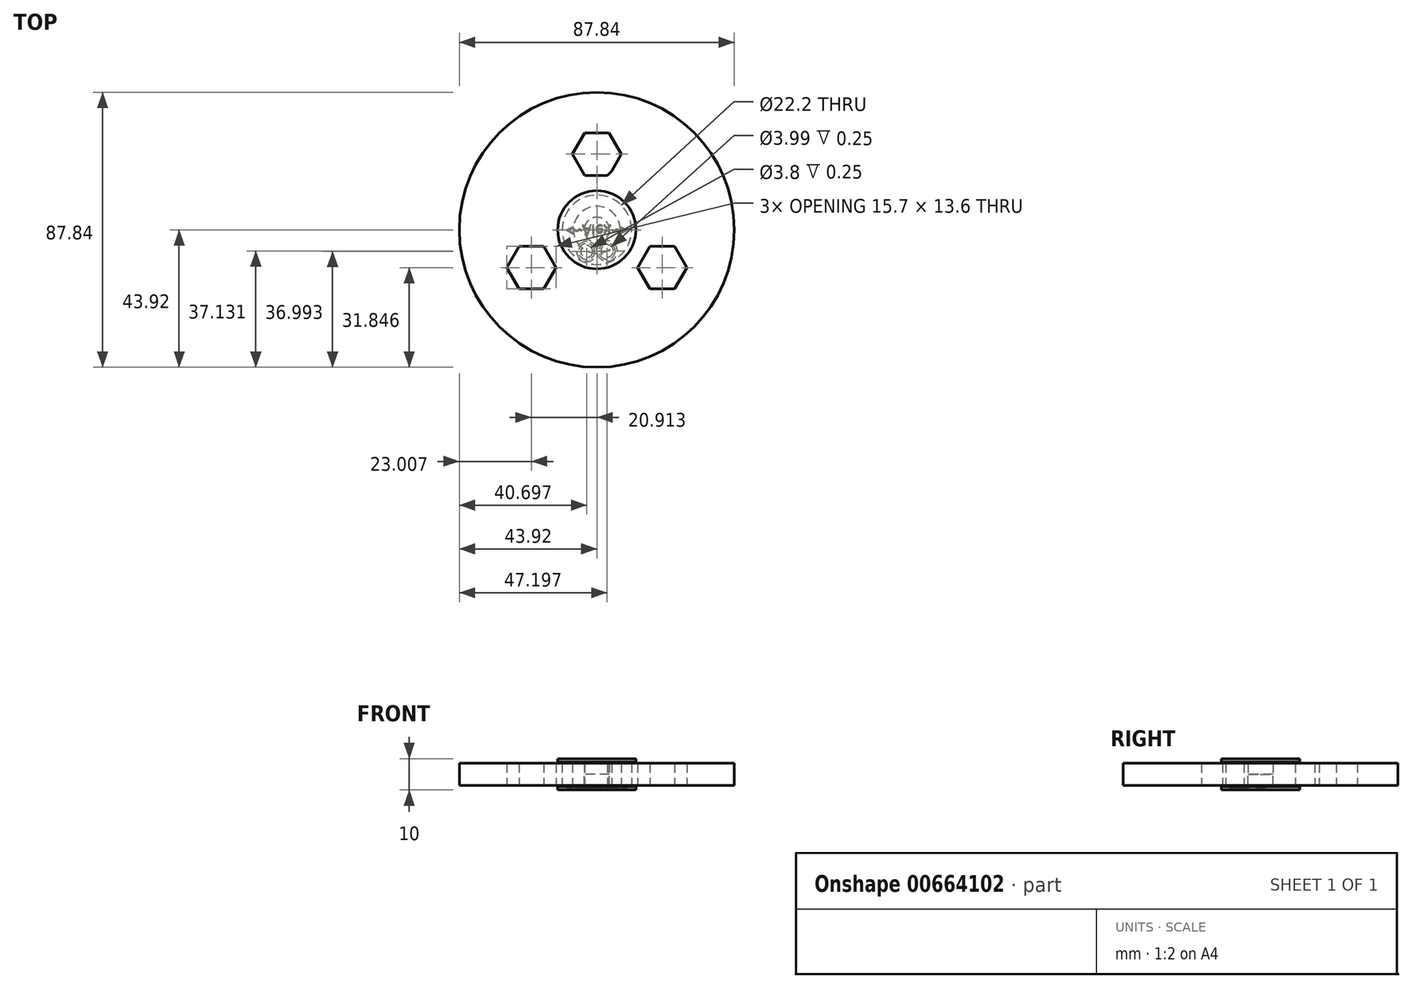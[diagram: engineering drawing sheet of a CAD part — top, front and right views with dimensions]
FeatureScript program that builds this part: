
annotation { "Feature Type Name" : "Feature", "Feature Type Description" : "" }
export const myFeature = defineFeature(function(context is Context, id is Id, definition is map)
    precondition{}
    {
        {
            var Q0;
            Q0=qCreatedBy(makeId("Top.planeOp"),FACE);
            var sketch = newSketch(context, id + "F0", { "sketchPlane" : qUnion([Q0])});
            skCircle(sketch, "E0", {"center": v(0, 0) * mm, "radius": 11.1 * mm});
            skCircle(sketch, "E1", {"center": v(0, 0) * mm, "radius": 4 * mm});
            skCircle(sketch, "E2.cCircle", {"center": v(0, 24.15) * mm, "radius": 6.8 * mm, "construction": true});
            skLineSegment(sketch, "E2.0", {"start": v(3.93, 17.35) * mm, "end": v(-3.93, 17.35) * mm});
            skLineSegment(sketch, "E2.1", {"start": v(-3.93, 17.35) * mm, "end": v(-7.85, 24.15) * mm});
            skLineSegment(sketch, "E2.2", {"start": v(-7.85, 24.15) * mm, "end": v(-3.93, 30.95) * mm});
            skLineSegment(sketch, "E2.3", {"start": v(-3.93, 30.95) * mm, "end": v(3.93, 30.95) * mm});
            skLineSegment(sketch, "E2.4", {"start": v(3.93, 30.95) * mm, "end": v(7.85, 24.15) * mm});
            skLineSegment(sketch, "E2.5", {"start": v(7.85, 24.15) * mm, "end": v(3.93, 17.35) * mm});
            skPoint(sketch, "E2.0.midPoint", {"position": v(0, 17.35) * mm});
            skLineSegment(sketch, "E3", {"start": v(0, 0) * mm, "end": v(0, 35) * mm, "construction": true});
            skArc(sketch, "E4", {"start": v(-11.18, 8.6) * mm, "mid": v(-12.21, 7.05) * mm, "end": v(-13.03, 5.38) * mm});
            skArc(sketch, "E5", {"start": v(-11.18, 8.6) * mm, "mid": v(-9, 13.96) * mm, "end": v(-9.89, 19.68) * mm});
            skArc(sketch, "E6", {"start": v(9.89, 19.68) * mm, "mid": v(9, 13.96) * mm, "end": v(11.18, 8.6) * mm});
            skArc(sketch, "E7.trimOffspring", {"start": v(9.89, 19.68) * mm, "mid": v(0, 35) * mm, "end": v(-9.89, 19.68) * mm});
            skArc(sketch, "E8.1.0", {"start": v(-1.86, -13.98) * mm, "mid": v(-7.59, -14.77) * mm, "end": v(-12.1, -18.4) * mm});
            skArc(sketch, "E8.1.1", {"start": v(-21.99, -1.28) * mm, "mid": v(-30.31, -17.5) * mm, "end": v(-12.1, -18.4) * mm});
            skLineSegment(sketch, "E8.1.2", {"start": v(-13.06, -12.07) * mm, "end": v(-16.99, -18.87) * mm});
            skLineSegment(sketch, "E8.1.3", {"start": v(-16.99, -18.87) * mm, "end": v(-24.84, -18.87) * mm});
            skLineSegment(sketch, "E8.1.4", {"start": v(-24.84, -18.87) * mm, "end": v(-28.76, -12.07) * mm});
            skLineSegment(sketch, "E8.1.5", {"start": v(-28.76, -12.07) * mm, "end": v(-24.84, -5.27) * mm});
            skLineSegment(sketch, "E8.1.6", {"start": v(-24.84, -5.27) * mm, "end": v(-16.99, -5.27) * mm});
            skLineSegment(sketch, "E8.1.7", {"start": v(-16.99, -5.27) * mm, "end": v(-13.06, -12.07) * mm});
            skArc(sketch, "E8.1.8", {"start": v(-21.99, -1.28) * mm, "mid": v(-16.59, 0.81) * mm, "end": v(-13.03, 5.38) * mm});
            skArc(sketch, "E8.2.0", {"start": v(13.03, 5.38) * mm, "mid": v(16.59, 0.81) * mm, "end": v(21.99, -1.28) * mm});
            skArc(sketch, "E8.2.1", {"start": v(12.1, -18.4) * mm, "mid": v(30.31, -17.5) * mm, "end": v(21.99, -1.28) * mm});
            skLineSegment(sketch, "E8.2.2", {"start": v(16.99, -5.27) * mm, "end": v(24.84, -5.27) * mm});
            skLineSegment(sketch, "E8.2.3", {"start": v(24.84, -5.27) * mm, "end": v(28.76, -12.07) * mm});
            skLineSegment(sketch, "E8.2.4", {"start": v(28.76, -12.07) * mm, "end": v(24.84, -18.87) * mm});
            skLineSegment(sketch, "E8.2.5", {"start": v(24.84, -18.87) * mm, "end": v(16.99, -18.87) * mm});
            skLineSegment(sketch, "E8.2.6", {"start": v(16.99, -18.87) * mm, "end": v(13.06, -12.07) * mm});
            skLineSegment(sketch, "E8.2.7", {"start": v(13.06, -12.07) * mm, "end": v(16.99, -5.27) * mm});
            skArc(sketch, "E8.2.8", {"start": v(12.1, -18.4) * mm, "mid": v(7.59, -14.77) * mm, "end": v(1.86, -13.98) * mm});
            skArc(sketch, "E9.trimOffspring", {"start": v(-1.86, -13.98) * mm, "mid": v(0, -14.1) * mm, "end": v(1.86, -13.98) * mm});
            skArc(sketch, "E10.trimOffspring", {"start": v(13.03, 5.38) * mm, "mid": v(12.21, 7.05) * mm, "end": v(11.18, 8.6) * mm});
            skArc(sketch, "E11", {"start": v(-13.03, 5.38) * mm, "mid": v(-14.09, 0.64) * mm, "end": v(-13.47, -4.18) * mm});
            skArc(sketch, "E12", {"start": v(11.18, 8.6) * mm, "mid": v(7.6, 11.88) * mm, "end": v(3.11, 13.75) * mm});
            skArc(sketch, "E13", {"start": v(1.86, -13.98) * mm, "mid": v(6.49, -12.52) * mm, "end": v(10.35, -9.57) * mm});
            skArc(sketch, "E14", {"start": v(-12.1, -18.4) * mm, "mid": v(-10.27, -14.18) * mm, "end": v(-10.35, -9.57) * mm});
            skArc(sketch, "E15", {"start": v(-9.89, 19.68) * mm, "mid": v(-7.14, 15.98) * mm, "end": v(-3.11, 13.75) * mm});
            skArc(sketch, "E16", {"start": v(21.99, -1.28) * mm, "mid": v(17.41, -1.8) * mm, "end": v(13.47, -4.18) * mm});
            skLineSegment(sketch, "E17", {"start": v(0, 24.15) * mm, "end": v(5.43, 33.55) * mm, "construction": true});
            skArc(sketch, "E18.trimOffspring", {"start": v(-13.47, -4.18) * mm, "mid": v(-17.41, -1.8) * mm, "end": v(-21.99, -1.28) * mm});
            skArc(sketch, "E19.trimOffspring", {"start": v(10.35, -9.57) * mm, "mid": v(10.27, -14.18) * mm, "end": v(12.1, -18.4) * mm});
            skArc(sketch, "E20.trimOffspring", {"start": v(3.11, 13.75) * mm, "mid": v(7.14, 15.98) * mm, "end": v(9.89, 19.68) * mm});
            skCircle(sketch, "E21", {"center": v(0, 0) * mm, "radius": 7.5 * mm});
            skCircle(sketch, "E22", {"center": v(0, 0) * mm, "radius": 12.5 * mm});
            skArc(sketch, "E23.trimOffspring", {"start": v(-3.11, 13.75) * mm, "mid": v(-7.6, 11.88) * mm, "end": v(-11.18, 8.6) * mm});
            skArc(sketch, "E24.trimOffspring", {"start": v(-10.35, -9.57) * mm, "mid": v(-6.49, -12.52) * mm, "end": v(-1.86, -13.98) * mm});
            skArc(sketch, "E25.trimOffspring", {"start": v(13.47, -4.18) * mm, "mid": v(14.09, 0.64) * mm, "end": v(13.03, 5.38) * mm});
            skSolve(sketch);
        }
        {
            var Q0;
            {var subQ1=sQuery(id+"F0.wireOp",EDGE,"E8.1.1");Q0=makeQuery(id+"F0.imprint","IMPRINT",FACE,{"disambiguationData":[TD([[makeQuery(id+"F0.imprint","IMPRINT",EDGE,{"derivedFrom":subQ1}),1.0]])]});}
            var Q1;
            {var subQ0=sQuery(id+"F0.wireOp",EDGE,"E8.1.8");Q1=makeQuery(id+"F0.imprint","IMPRINT",FACE,{"disambiguationData":[TD([[makeQuery(id+"F0.imprint","IMPRINT",EDGE,{"derivedFrom":subQ0}),-1.0]])]});}
            var Q2;
            Q2=makeQuery(id+"F0.imprint","IMPRINT",FACE,{"disambiguationData":[TD([[makeQuery(id+"F0.imprint","IMPRINT",EDGE,{"derivedFrom":sQuery(id+"F0.wireOp",EDGE,"E0")}),-1.0]])]});
            var Q3;
            {var subQ0=sQuery(id+"F0.wireOp",EDGE,"E5");Q3=makeQuery(id+"F0.imprint","IMPRINT",FACE,{"disambiguationData":[TD([[makeQuery(id+"F0.imprint","IMPRINT",EDGE,{"derivedFrom":subQ0}),-1.0]])]});}
            var Q4;
            Q4=makeQuery(id+"F0.imprint","IMPRINT",FACE,{"disambiguationData":[TD([[makeQuery(id+"F0.imprint","IMPRINT",EDGE,{"derivedFrom":sQuery(id+"F0.wireOp",EDGE,"E2.0")}),1.0]])]});
            var Q5;
            {var subQ0=sQuery(id+"F0.wireOp",EDGE,"E8.1.0");Q5=makeQuery(id+"F0.imprint","IMPRINT",FACE,{"disambiguationData":[TD([[makeQuery(id+"F0.imprint","IMPRINT",EDGE,{"derivedFrom":subQ0}),-1.0]])]});}
            var Q6;
            {var subQ0=sQuery(id+"F0.wireOp",EDGE,"E8.2.0");Q6=makeQuery(id+"F0.imprint","IMPRINT",FACE,{"disambiguationData":[TD([[makeQuery(id+"F0.imprint","IMPRINT",EDGE,{"derivedFrom":subQ0}),-1.0]])]});}
            var Q7;
            {var subQ0=sQuery(id+"F0.wireOp",EDGE,"E8.2.8");Q7=makeQuery(id+"F0.imprint","IMPRINT",FACE,{"disambiguationData":[TD([[makeQuery(id+"F0.imprint","IMPRINT",EDGE,{"derivedFrom":subQ0}),-1.0]])]});}
            var Q8;
            {var subQ0=sQuery(id+"F0.wireOp",EDGE,"E8.2.1");Q8=makeQuery(id+"F0.imprint","IMPRINT",FACE,{"disambiguationData":[TD([[makeQuery(id+"F0.imprint","IMPRINT",EDGE,{"derivedFrom":subQ0}),1.0]])]});}
            var Q9;
            {var subQ0=sQuery(id+"F0.wireOp",EDGE,"E6");Q9=makeQuery(id+"F0.imprint","IMPRINT",FACE,{"disambiguationData":[TD([[makeQuery(id+"F0.imprint","IMPRINT",EDGE,{"derivedFrom":subQ0}),-1.0]])]});}
            var Q10;
            {var subQ4=sQuery(id+"F0.wireOp",EDGE,"E4");Q10=makeQuery(id+"F0.imprint","IMPRINT",FACE,{"disambiguationData":[TD([[makeQuery(id+"F0.imprint","IMPRINT",EDGE,{"derivedFrom":subQ4}),1.0]])]});}
            extrude(context, id + "F1", {"entities" : qUnion([Q0, Q1, Q2, Q3, Q4, Q5, Q6, Q7, Q8, Q9, Q10]), "endBound" : BoundingType.SYMMETRIC, "depth" : 3 * mm, "offsetDistance" : 25 * mm});
        }
        {
            var Q0;
            Q0=makeQuery(id+"F0.imprint","IMPRINT",FACE,{"disambiguationData":[TD([[makeQuery(id+"F0.imprint","IMPRINT",EDGE,{"derivedFrom":sQuery(id+"F0.wireOp",EDGE,"E0")}),-1.0]])]});
            var Q1;
            Q1=makeQuery(id+"F0.imprint","IMPRINT",FACE,{"disambiguationData":[TD([[makeQuery(id+"F0.imprint","IMPRINT",EDGE,{"derivedFrom":sQuery(id+"F0.wireOp",EDGE,"E2.0")}),1.0]])]});
            extrude(context, id + "F2", {"entities" : qUnion([Q0, Q1]), "operationType" : NewBodyOperationType.ADD, "endBound" : BoundingType.SYMMETRIC, "oppositeDirection" : true, "depth" : 7 * mm, "offsetDistance" : 25 * mm});
        }
        {
            var Q0;
            Q0=makeQuery(id+"F0.imprint","IMPRINT",FACE,{"disambiguationData":[TD([[makeQuery(id+"F0.imprint","IMPRINT",EDGE,{"derivedFrom":sQuery(id+"F0.wireOp",EDGE,"E1")}),1.0]])]});
            extrude(context, id + "F3", {"entities" : qUnion([Q0]), "depth" : 3.5 * mm, "offsetDistance" : 25 * mm});
        }
        {
            var Q0;
            Q0=makeQuery(id+"F0.imprint","IMPRINT",FACE,{"disambiguationData":[TD([[makeQuery(id+"F0.imprint","IMPRINT",EDGE,{"derivedFrom":sQuery(id+"F0.wireOp",EDGE,"E1")}),1.0]])]});
            var Q1;
            Q1=makeQuery(id+"F0.imprint","IMPRINT",FACE,{"disambiguationData":[TD([[makeQuery(id+"F0.imprint","IMPRINT",EDGE,{"derivedFrom":sQuery(id+"F0.wireOp",EDGE,"E1")}),-1.0]])]});
            var Q2;
            Q2=makeQuery(id+"F3.opExtrude","CAP_FACE",FACE,{"disambiguationData":[OSD([sQuery(id+"F0.wireOp",EDGE,"E1")])],"isStart":false});
            extrude(context, id + "F4", {"entities" : qUnion([Q0, Q1]), "operationType" : NewBodyOperationType.ADD, "depth" : 4 * mm, "offsetDistance" : 25 * mm, "hasSecondDirection" : true, "secondDirectionBound" : SecondDirectionBoundingType.UP_TO_SURFACE, "secondDirectionOppositeDirection" : false, "secondDirectionDepth" : 25 * mm, "secondDirectionBoundEntityFace" : qUnion([Q2])});
        }
        {
            var Q0;
            Q0=makeQuery(id+"F0.imprint","IMPRINT",FACE,{"disambiguationData":[TD([[makeQuery(id+"F0.imprint","IMPRINT",EDGE,{"derivedFrom":sQuery(id+"F0.wireOp",EDGE,"E0")}),-1.0]])]});
            var Q1;
            Q1=makeQuery(id+"F0.imprint","IMPRINT",FACE,{"disambiguationData":[TD([[makeQuery(id+"F0.imprint","IMPRINT",EDGE,{"derivedFrom":sQuery(id+"F0.wireOp",EDGE,"E0")}),1.0]])]});
            var Q2;
            Q2=makeQuery(id+"F0.imprint","IMPRINT",FACE,{"disambiguationData":[TD([[makeQuery(id+"F0.imprint","IMPRINT",EDGE,{"derivedFrom":sQuery(id+"F0.wireOp",EDGE,"E1")}),-1.0]])]});
            var Q3;
            Q3=makeQuery(id+"F0.imprint","IMPRINT",FACE,{"disambiguationData":[TD([[makeQuery(id+"F0.imprint","IMPRINT",EDGE,{"derivedFrom":sQuery(id+"F0.wireOp",EDGE,"E1")}),1.0]])]});
            var Q4;
            Q4=makeQuery(id+"F4.opExtrude","CAP_FACE",FACE,{"disambiguationData":[OSD([sQuery(id+"F0.wireOp",EDGE,"E21")])],"isStart":false});
            extrude(context, id + "F5", {"entities" : qUnion([Q0, Q1, Q2, Q3]), "operationType" : NewBodyOperationType.ADD, "depth" : 5 * mm, "offsetDistance" : 25 * mm, "hasSecondDirection" : true, "secondDirectionBound" : SecondDirectionBoundingType.UP_TO_SURFACE, "secondDirectionOppositeDirection" : false, "secondDirectionDepth" : 25 * mm, "secondDirectionBoundEntityFace" : qUnion([Q4])});
        }
        {
            var Q0;
            Q0=makeQuery(id+"F3.opExtrude","SWEPT_BODY",BODY,{"disambiguationData":[OSD([sQuery(id+"F0.wireOp",EDGE,"E1")])]});
            var Q1;
            Q1=makeQuery(id+"F3.opExtrude","CAP_FACE",FACE,{"disambiguationData":[OSD([sQuery(id+"F0.wireOp",EDGE,"E1")])],"isStart":true});
            mirror(context, id + "F6", {"entities" : qUnion([Q0]), "mirrorPlane" : qUnion([Q1])});
        }
        {
            var Q0;
            Q0=makeQuery(id+"F6.opPattern","COPY",FACE,{"derivedFrom":makeQuery(id+"F5.opExtrude","CAP_FACE",FACE,{"disambiguationData":[OSD([sQuery(id+"F0.wireOp",EDGE,"E22")])],"isStart":false}),"instanceName":"1"});
            var sketch = newSketch(context, id + "F7", { "sketchPlane" : qUnion([Q0])});
            skText(sketch, "E26", { "text": "<~Alex~>", "fontName": "OpenSans-Regular.ttf"});
            skPoint(sketch, "E27", {"position": v(0, -12.5) * mm});
            skPoint(sketch, "E28", {"position": v(-12.5, 0) * mm});
            const initialGuessF7  = {"E26": [-0.01, -0.0015, 1, 0, 0.00337]};
            skSetInitialGuess(sketch, initialGuessF7);
            skSolve(sketch);
        }
        {
            var Q0;
            Q0=makeQuery(id+"F7.imprint","IMPRINT",FACE,{"disambiguationData":[TD([[makeQuery(id+"F7.imprint","IMPRINT",EDGE,{"derivedFrom":sQuery(id+"F7.wireOp",EDGE,"E26.sketch_text.stroke-0")}),1.0]])]});
            var sketch = newSketch(context, id + "F8", { "sketchPlane" : qUnion([Q0])});
            skArc(sketch, "E29", {"start": v(0.04, 6.25) * mm, "mid": v(6.55, 6.67) * mm, "end": v(0.1, 7.57) * mm});
            skPoint(sketch, "E30.center.orphan", {"position": v(0, 6.93) * mm});
            skCircle(sketch, "E31", {"center": v(-3.22, 6.93) * mm, "radius": 2.57 * mm});
            skCircle(sketch, "E32", {"center": v(3.28, 6.79) * mm, "radius": 2.62 * mm});
            skLineSegment(sketch, "E33.trimOffspring", {"start": v(-0.07, 7.62) * mm, "end": v(-0.07, 7.62) * mm});
            skPoint(sketch, "E34.1.internal.orphan", {"position": v(0.1, 7.15) * mm});
            skArc(sketch, "E35", {"start": v(-0.07, 7.62) * mm, "mid": v(-6.45, 6.97) * mm, "end": v(-0.1, 6.14) * mm});
            skFitSpline(sketch, "E36", {"points": [v(-0.07, 7.62) * mm, v(0, 7.34) * mm, v(0.1, 7.57) * mm, v(0.3, 7.07) * mm, v(0.3, 6.56) * mm, v(0.3, 6.34) * mm], "startDerivative": vector(0.4, -2.54) * mm, "endDerivative": vector(0.05, -1.27) * mm});
            skFitSpline(sketch, "E37", {"points": [v(-0.1, 6.14) * mm, v(0, 6.43) * mm, v(0.04, 6.25) * mm], "startDerivative": vector(0.2, 0.78) * mm, "endDerivative": vector(0.08, -0.63) * mm});
            skPoint(sketch, "E38.3.internal.orphan", {"position": v(0.04, 6.93) * mm});
            skPoint(sketch, "E38.4.internal.orphan", {"position": v(-0.1, 7.15) * mm});
            skPoint(sketch, "E38.endDerivative.orphan", {"position": v(0.3, 6.89) * mm});
            skCircle(sketch, "E39", {"center": v(-3.22, 6.93) * mm, "radius": 1.9 * mm});
            skCircle(sketch, "E40", {"center": v(3.28, 6.79) * mm, "radius": 2 * mm});
            skLineSegment(sketch, "E41", {"start": v(-12.67, 0) * mm, "end": v(21.78, 0) * mm});
            skLineSegment(sketch, "E42", {"start": v(21.78, 0) * mm, "end": v(16.86, 11.11) * mm});
            skArc(sketch, "E43.MirrorCS", {"start": v(0.04, -6.25) * mm, "mid": v(6.55, -6.67) * mm, "end": v(0.1, -7.57) * mm});
            skArc(sketch, "E44.MirrorCS", {"start": v(-0.07, -7.62) * mm, "mid": v(-6.45, -6.97) * mm, "end": v(-0.1, -6.14) * mm});
            skCircle(sketch, "E45.MirrorC", {"center": v(-3.22, -6.93) * mm, "radius": 2.57 * mm});
            skCircle(sketch, "E46.MirrorC", {"center": v(-3.22, -6.93) * mm, "radius": 1.9 * mm});
            skCircle(sketch, "E47.MirrorC", {"center": v(3.28, -6.79) * mm, "radius": 2 * mm});
            skCircle(sketch, "E48.MirrorC", {"center": v(3.28, -6.79) * mm, "radius": 2.62 * mm});
            skFitSpline(sketch, "E49.MirrorCS", {"points": [v(-0.1, -6.14) * mm, v(0, -6.43) * mm, v(0.04, -6.25) * mm], "startDerivative": vector(0.2, -0.78) * mm, "endDerivative": vector(0.08, 0.63) * mm});
            skFitSpline(sketch, "E50.MirrorCS", {"points": [v(-0.07, -7.62) * mm, v(0, -7.34) * mm, v(0.1, -7.57) * mm, v(0.3, -7.07) * mm, v(0.3, -6.56) * mm, v(0.3, -6.34) * mm], "startDerivative": vector(0.4, 2.54) * mm, "endDerivative": vector(0.05, 1.27) * mm});
            skSolve(sketch);
        }
        {
            var Q0;
            Q0=makeQuery(id+"F8.imprint","IMPRINT",FACE,{"disambiguationData":[TD([[makeQuery(id+"F8.imprint","IMPRINT",EDGE,{"derivedFrom":sQuery(id+"F8.wireOp",EDGE,"E40")}),1.0]])]});
            var Q1;
            Q1=makeQuery(id+"F8.imprint","IMPRINT",FACE,{"disambiguationData":[TD([[makeQuery(id+"F8.imprint","IMPRINT",EDGE,{"derivedFrom":sQuery(id+"F8.wireOp",EDGE,"E29")}),1.0]])]});
            var Q2;
            Q2=makeQuery(id+"F8.imprint","IMPRINT",FACE,{"disambiguationData":[TD([[makeQuery(id+"F8.imprint","IMPRINT",EDGE,{"derivedFrom":sQuery(id+"F8.wireOp",EDGE,"E39")}),1.0]])]});
            extrude(context, id + "F9", {"entities" : qUnion([Q0, Q1, Q2]), "operationType" : NewBodyOperationType.REMOVE, "oppositeDirection" : true, "depth" : .25 * mm, "offsetDistance" : 25 * mm});
        }
        {
            var Q0;
            Q0 = qSketchRegion(id + "F7", true);
            extrude(context, id + "F10", {"entities" : qUnion([Q0]), "operationType" : NewBodyOperationType.REMOVE, "oppositeDirection" : true, "depth" : .25 * mm, "offsetDistance" : 25 * mm});
        }
        {
            var Q0;
            Q0=qCreatedBy(makeId("Top.planeOp"),FACE);
            var sketch = newSketch(context, id + "F11", { "sketchPlane" : qUnion([Q0])});
            skFitSpline(sketch, "E51", {"points": [v(10.44, 24.14) * mm, v(8.47, 14.54) * mm, v(13.87, 0) * mm, v(17.82, 0) * mm, v(24.67, 0) * mm, v(31.02, -10.75) * mm, v(30.16, -18.9) * mm, v(23.73, -20.7) * mm, v(14.13, -19.32) * mm, v(11.82, -16.15) * mm, v(8.13, -13.24) * mm, v(0, -13.15) * mm, v(-10.47, -13.58) * mm, v(-14.93, -19.32) * mm, v(-25.56, -20.35) * mm, v(-29.93, -11.44) * mm, v(-26.08, -4.06) * mm, v(-15.96, 0) * mm, v(-7.39, 13.94) * mm, v(-9.62, 23.97) * mm, v(-4.73, 32.28) * mm, v(0, 32.71) * mm, v(5.9, 32.2) * mm, v(10.44, 24.14) * mm]});
            skFitSpline(sketch, "E52", {"points": [v(-15.81, 42.22) * mm, v(51.8, 40.54) * mm, v(46.07, -43.82) * mm, v(-39.37, -51.4) * mm, v(-45.4, 26.76) * mm, v(-15.81, 42.22) * mm]});
            skSolve(sketch);
        }
        {
            var Q0;
            Q0=makeQuery(id+"F11.imprint","IMPRINT",FACE,{"disambiguationData":[TD([[makeQuery(id+"F11.imprint","IMPRINT",EDGE,{"derivedFrom":sQuery(id+"F11.wireOp",EDGE,"E51")}),1.0]])]});
            extrude(context, id + "F12", {"entities" : qUnion([Q0]), "operationType" : NewBodyOperationType.ADD, "depth" : 3.5 * mm, "offsetDistance" : 25 * mm, "hasSecondDirection" : true, "secondDirectionOppositeDirection" : true, "secondDirectionDepth" : 3.5 * mm});
        }
        {
            var Q0;
            Q0=qCreatedBy(makeId("Top.planeOp"),FACE);
            var sketch = newSketch(context, id + "F13", { "sketchPlane" : qUnion([Q0])});
            skFitSpline(sketch, "E53", {"points": [v(-25.09, 0) * mm, v(-14.35, -5.2) * mm, v(-11.22, -15.94) * mm, v(0, -23.88) * mm, v(7.56, -22.09) * mm, v(12.03, -9.9) * mm, v(16.62, -3.98) * mm, v(28.36, -5.32) * mm, v(30.48, -14.7) * mm, v(25.23, -20.86) * mm, v(37.64, -20.52) * mm], "startDerivative": vector(125.02, -33) * mm, "endDerivative": vector(170.09, 21.27) * mm});
            skFitSpline(sketch, "E54", {"points": [v(-13.12, 7.76) * mm, v(-10.1, -5.2) * mm, v(0, -15.94) * mm, v(12.03, -5.2) * mm, v(12.03, 0) * mm, v(12.03, 7.54) * mm, v(0, 11.34) * mm, v(-13.12, 7.76) * mm]});
            skPoint(sketch, "E55.1.internal.orphan", {"position": v(42, 0) * mm});
            skPoint(sketch, "E55.5.internal.orphan", {"position": v(0, 15.48) * mm});
            skFitSpline(sketch, "E56", {"points": [v(-25.09, 0) * mm, v(-18.56, 21.41) * mm, v(0, 15.48) * mm, v(16.77, 30.45) * mm, v(42, 0) * mm, v(37.64, -20.52) * mm], "startDerivative": vector(12.87, 163.32) * mm, "endDerivative": vector(-53.42, -92.17) * mm});
            skSolve(sketch);
        }
        {
            var Q0;
            Q0 = qSketchRegion(id + "F13", true);
            extrude(context, id + "F14", {"entities" : qUnion([Q0]), "operationType" : NewBodyOperationType.ADD, "depth" : 3.5 * mm, "offsetDistance" : 25 * mm, "hasSecondDirection" : true, "secondDirectionOppositeDirection" : true, "secondDirectionDepth" : 3.5 * mm});
        }
        {
            var Q0;
            Q0=qCreatedBy(makeId("Top.planeOp"),FACE);
            var sketch = newSketch(context, id + "F15", { "sketchPlane" : qUnion([Q0])});
            skFitSpline(sketch, "E57", {"points": [v(2.61, -14.25) * mm, v(8.47, -15.43) * mm, v(8.17, -10.3) * mm, v(2.61, -14.25) * mm]});
            skSolve(sketch);
        }
        {
            var Q0;
            Q0 = qSketchRegion(id + "F15", true);
            extrude(context, id + "F16", {"entities" : qUnion([Q0]), "operationType" : NewBodyOperationType.ADD, "depth" : 3.5 * mm, "offsetDistance" : 25 * mm, "hasSecondDirection" : true, "secondDirectionOppositeDirection" : true, "secondDirectionDepth" : 3.5 * mm});
        }
        {
            var Q0;
            Q0=qCreatedBy(makeId("Top.planeOp"),FACE);
            var sketch = newSketch(context, id + "F17", { "sketchPlane" : qUnion([Q0])});
            skCircle(sketch, "E58", {"center": v(0, 0) * mm, "radius": 43.92 * mm});
            skCircle(sketch, "E59", {"center": v(0, 0) * mm, "radius": 70.15 * mm});
            skSolve(sketch);
        }
        {
            var Q0;
            Q0 = qSketchRegion(id + "F17", true);
            extrude(context, id + "F18", {"entities" : qUnion([Q0]), "operationType" : NewBodyOperationType.REMOVE, "oppositeDirection" : true, "depth" : 25 * mm, "offsetDistance" : 25 * mm, "hasSecondDirection" : true, "secondDirectionOppositeDirection" : false, "secondDirectionDepth" : 25 * mm});
        }
    });
